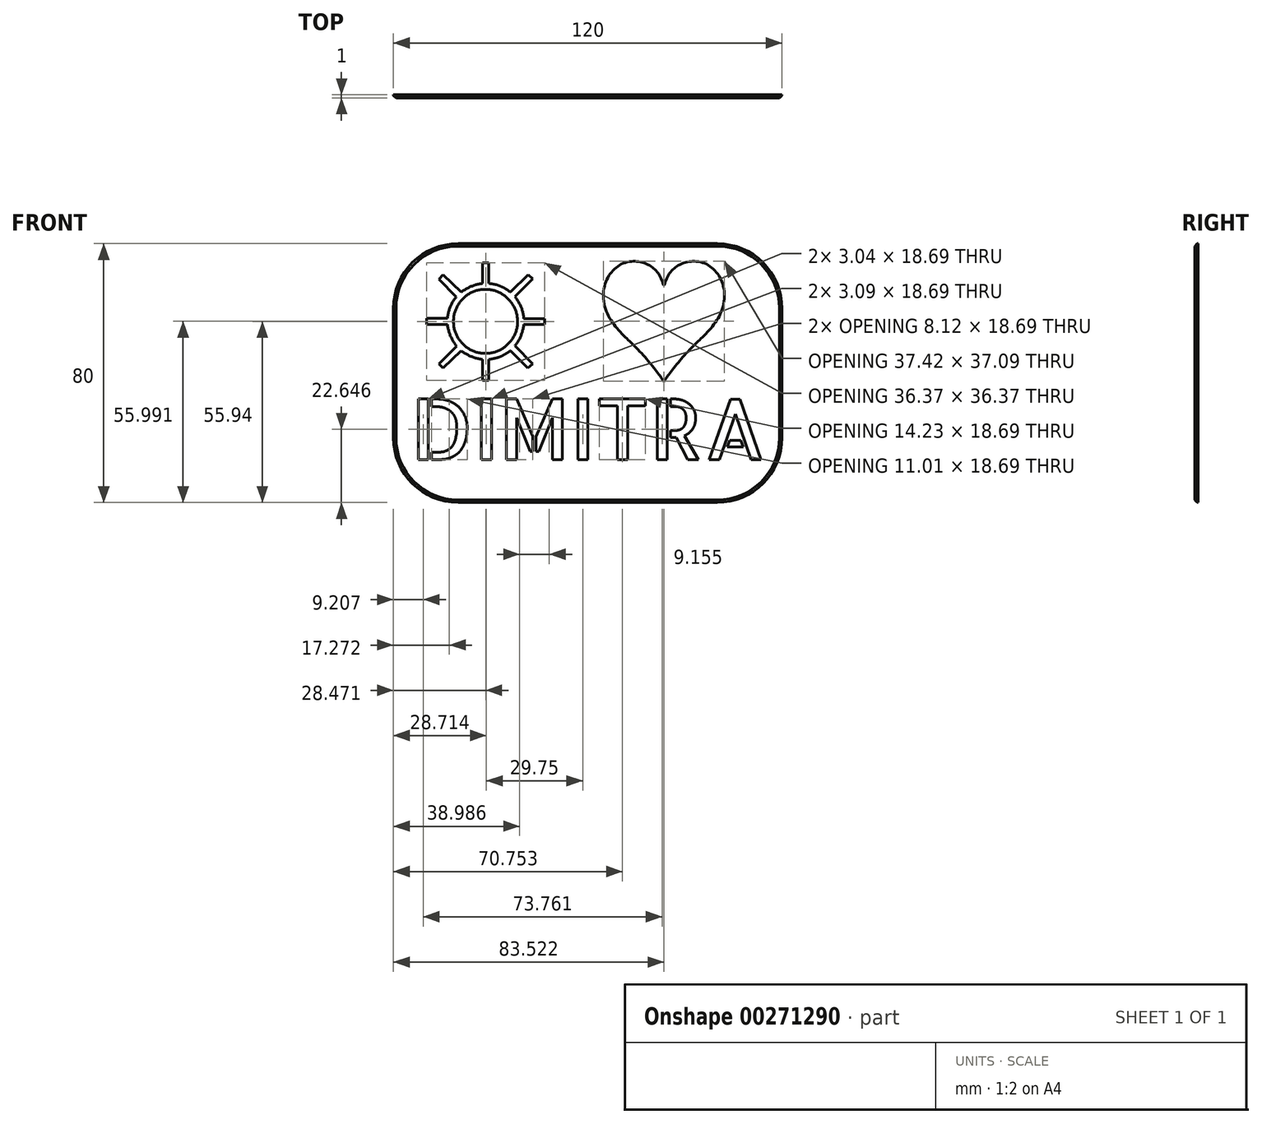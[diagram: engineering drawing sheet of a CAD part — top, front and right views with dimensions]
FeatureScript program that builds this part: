
annotation { "Feature Type Name" : "Feature", "Feature Type Description" : "" }
export const myFeature = defineFeature(function(context is Context, id is Id, definition is map)
    precondition{}
    {
        {
            var Q0;
            Q0=qCreatedBy(makeId("Front.planeOp"),FACE);
            var sketch = newSketch(context, id + "F0", { "sketchPlane" : qUnion([Q0])});
            skLineSegment(sketch, "E0.bottom", {"start": v(-60, 60) * mm, "end": v(60, 60) * mm});
            skLineSegment(sketch, "E0.top", {"start": v(-60, -20) * mm, "end": v(60, -20) * mm});
            skLineSegment(sketch, "E0.left", {"start": v(-60, 60) * mm, "end": v(-60, -20) * mm});
            skLineSegment(sketch, "E0.right", {"start": v(60, 60) * mm, "end": v(60, -20) * mm});
            skSolve(sketch);
        }
        {
            var Q0;
            Q0 = qSketchRegion(id + "F0", true);
            extrude(context, id + "F1", {"entities" : qUnion([Q0]), "depth" : 1 * mm});
        }
        {
            var Q0;
            Q0=makeQuery(id+"F1.opExtrude","CAP_FACE",FACE,{"disambiguationData":[OSD([sQuery(id+"F0.wireOp",EDGE,"E0.bottom"),sQuery(id+"F0.wireOp",EDGE,"E0.top"),sQuery(id+"F0.wireOp",EDGE,"E0.left"),sQuery(id+"F0.wireOp",EDGE,"E0.right")])],"isStart":false});
            var sketch = newSketch(context, id + "F2", { "sketchPlane" : qUnion([Q0])});
            skText(sketch, "E1", { "text": "DIMITRA", "fontName": "AllertaStencil-Regular.ttf"});
            skText(sketch, "E2", { "text": "☼", "fontName": "NotoSerif-Bold.ttf"});
            skText(sketch, "E3", { "text": "♥", "fontName": "NotoSansCJKjp-Regular.otf"});
            const initialGuessF2  = {"E1": [-0.05475, -0.0067, 1, 0, 0.0187], "E2": [-0.0594, 0.02195, 1, 0, 0.04381], "E3": [0.0013, 0.01916, 1, 0, 0.032]};
            skSetInitialGuess(sketch, initialGuessF2);
            skSolve(sketch);
        }
        {
            var Q0;
            Q0 = qSketchRegion(id + "F2", true);
            extrude(context, id + "F3", {"entities" : qUnion([Q0]), "operationType" : NewBodyOperationType.REMOVE, "endBound" : BoundingType.THROUGH_ALL, "oppositeDirection" : true, "depth" : 25 * mm});
        }
        {
            var Q0;
            Q0=makeQuery(id+"F1.opExtrude","SWEPT_EDGE",EDGE,{"disambiguationData":[OSD([sQuery(id+"F0.wireOp",EDGE,"E0.top"),sQuery(id+"F0.wireOp",EDGE,"E0.right")])]});
            var Q1;
            Q1=makeQuery(id+"F1.opExtrude","SWEPT_EDGE",EDGE,{"disambiguationData":[OSD([sQuery(id+"F0.wireOp",EDGE,"E0.bottom"),sQuery(id+"F0.wireOp",EDGE,"E0.right")])]});
            var Q2;
            Q2=makeQuery(id+"F1.opExtrude","SWEPT_EDGE",EDGE,{"disambiguationData":[OSD([sQuery(id+"F0.wireOp",EDGE,"E0.top"),sQuery(id+"F0.wireOp",EDGE,"E0.left")])]});
            var Q3;
            Q3=makeQuery(id+"F1.opExtrude","SWEPT_EDGE",EDGE,{"disambiguationData":[OSD([sQuery(id+"F0.wireOp",EDGE,"E0.bottom"),sQuery(id+"F0.wireOp",EDGE,"E0.left")])]});
            fillet(context, id + "F4", {"entities" : qUnion([Q0, Q1, Q2, Q3]), "radius" : 20 * mm, "tangentPropagation" : true, "allowEdgeOverflow" : false});
        }
        {
            var Q0;
            Q0=makeQuery(id+"F1.opExtrude","CAP_EDGE",EDGE,{"disambiguationData":[OSD([sQuery(id+"F0.wireOp",EDGE,"E0.top")])],"isStart":false});
            chamfer(context, id + "F5", {"entities" : qUnion([Q0]), "width" : 0.8 * mm, "tangentPropagation" : true});
        }
    });
